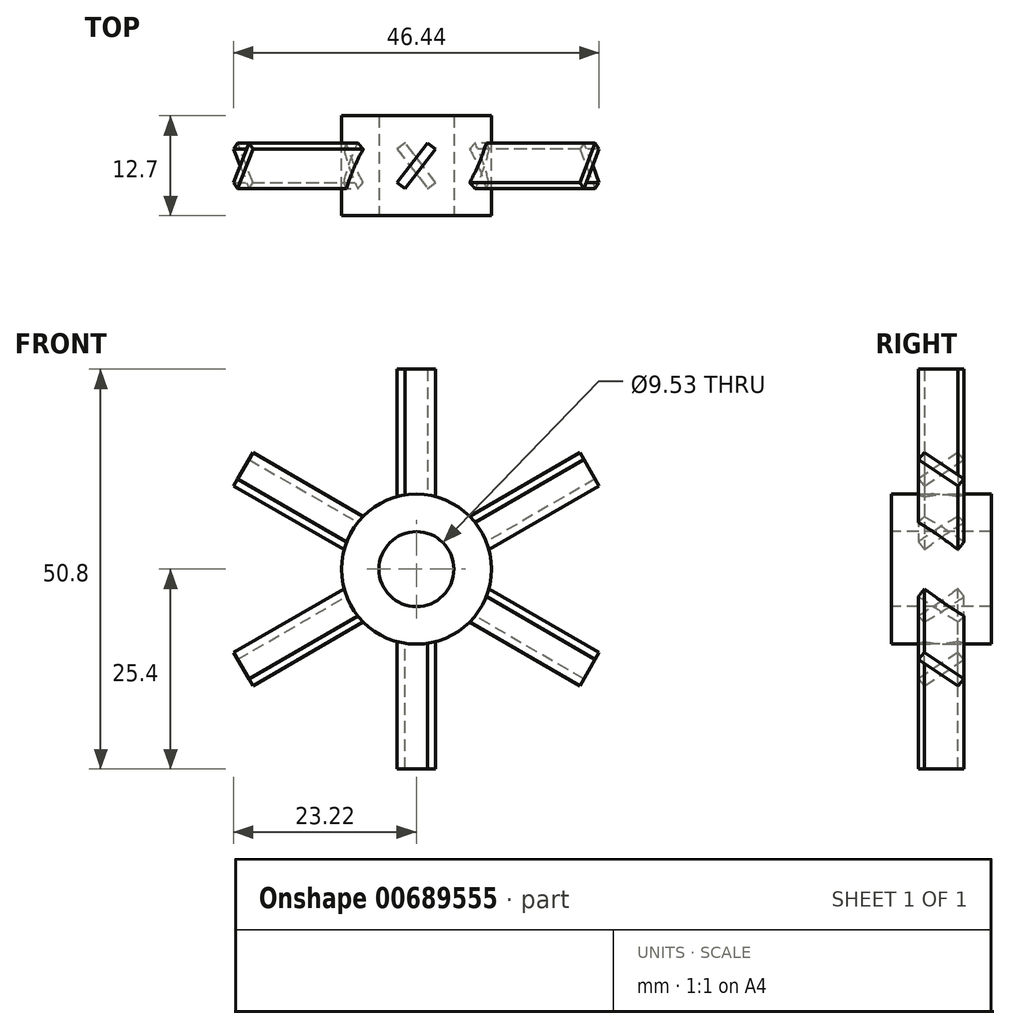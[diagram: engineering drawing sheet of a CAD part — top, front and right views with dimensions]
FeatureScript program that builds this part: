
annotation { "Feature Type Name" : "Feature", "Feature Type Description" : "" }
export const myFeature = defineFeature(function(context is Context, id is Id, definition is map)
    precondition{}
    {
        {
            var Q0;
            Q0=qCreatedBy(makeId("Top.planeOp"),FACE);
            var sketch = newSketch(context, id + "F0", { "sketchPlane" : qUnion([Q0])});
            skLineSegment(sketch, "E0", {"start": v(1.43, 2.9) * mm, "end": v(2.44, 2.13) * mm});
            skLineSegment(sketch, "E1", {"start": v(2.44, 2.13) * mm, "end": v(-1.43, -2.9) * mm});
            skLineSegment(sketch, "E2", {"start": v(-1.43, -2.9) * mm, "end": v(-2.44, -2.13) * mm});
            skLineSegment(sketch, "E3", {"start": v(-2.44, -2.13) * mm, "end": v(1.43, 2.9) * mm});
            skSolve(sketch);
        }
        {
            var Q0;
            Q0 = qSketchRegion(id + "F0", true);
            extrude(context, id + "F1", {"entities" : qUnion([Q0]), "depth" : 25.4 * mm, "offsetDistance" : 25.4 * mm});
        }
        {
            var Q0;
            Q0=qCreatedBy(makeId("Right.planeOp"),FACE);
            var sketch = newSketch(context, id + "F2", { "sketchPlane" : qUnion([Q0])});
            skLineSegment(sketch, "E4", {"start": v(0, 0) * mm, "end": v(38.1, 0) * mm});
            skSolve(sketch);
        }
        {
            var Q0;
            Q0=makeQuery(id+"F1.opExtrude","SWEPT_BODY",BODY,{"disambiguationData":[OSD([sQuery(id+"F0.wireOp",EDGE,"E0"),sQuery(id+"F0.wireOp",EDGE,"E1"),sQuery(id+"F0.wireOp",EDGE,"E2"),sQuery(id+"F0.wireOp",EDGE,"E3")])]});
            var Q1;
            Q1=sQuery(id+"F2.wireOp",EDGE,"E4");
            circularPattern(context, id + "F3", {"entities" : qUnion([Q0]), "axis" : qUnion([Q1]), "angle" : 360 * degree, "instanceCount" : 6, "equalSpace" : true});
        }
        {
            var Q0;
            Q0=qCreatedBy(makeId("Front.planeOp"),FACE);
            var sketch = newSketch(context, id + "F4", { "sketchPlane" : qUnion([Q0])});
            skCircle(sketch, "E5", {"center": v(0, 0) * mm, "radius": 9.53 * mm});
            skSolve(sketch);
        }
        {
            var Q0;
            Q0 = qSketchRegion(id + "F4", true);
            extrude(context, id + "F5", {"entities" : qUnion([Q0]), "operationType" : NewBodyOperationType.ADD, "endBound" : BoundingType.SYMMETRIC, "depth" : 12.7 * mm, "offsetDistance" : 25.4 * mm});
        }
        {
            var Q0;
            Q0=makeQuery(id+"F5.opExtrude","CAP_FACE",FACE,{"disambiguationData":[OSD([sQuery(id+"F4.wireOp",EDGE,"E5")])],"isStart":false});
            var sketch = newSketch(context, id + "F6", { "sketchPlane" : qUnion([Q0])});
            skCircle(sketch, "E6", {"center": v(0, 0) * mm, "radius": 4.76 * mm});
            skSolve(sketch);
        }
        {
            var Q0;
            Q0 = qSketchRegion(id + "F6", true);
            extrude(context, id + "F7", {"entities" : qUnion([Q0]), "operationType" : NewBodyOperationType.REMOVE, "oppositeDirection" : true, "depth" : 12.7 * mm, "offsetDistance" : 25.4 * mm});
        }
    });
